# Revit family: Sink-Corian-European-Sweet-881
name_source: partatom
category: Plumbing Fixtures
revit_build: Autodesk Revit 2015 (Build: 20140606_1530(x64)
units: mm (PartAtom-declared; Revit-internal decimal feet)

## types (1)
- 881
    CWFU = 0
    Cost = 0 $
    Default Elevation = 1219 mm
    Depth = 229 mm
    Description = Kitchen Sink Europe Specification
    Finish = Solid Surface Sink - DuPont - Bone
    HWFU = 0
    Interior Length = 436 mm  [stored 1.43045 ft]
    Interior Width = 695 mm  [stored 2.28018 ft]
    Length = 474 mm  [stored 1.55512 ft]
    Manufacturer = DuPont
    Model = Sweet 881
    Product Page URL = http://www.corian.uk
    Sink Colors Available = Bone, Cameo White, Designer White, Glacier White, Vanilla
    URL = http://www.corian.uk
    Version = 2015 - v1.0b
    WFU = 0
    Width = 733 mm  [stored 2.40486 ft]

note: [stored X ft] marks values corroborated as IEEE doubles in the binary element streams (Revit-internal decimal feet)

## geometry (parser evidence)
native form markers: Sweep x2
no freeform markers — native parametric forms only
